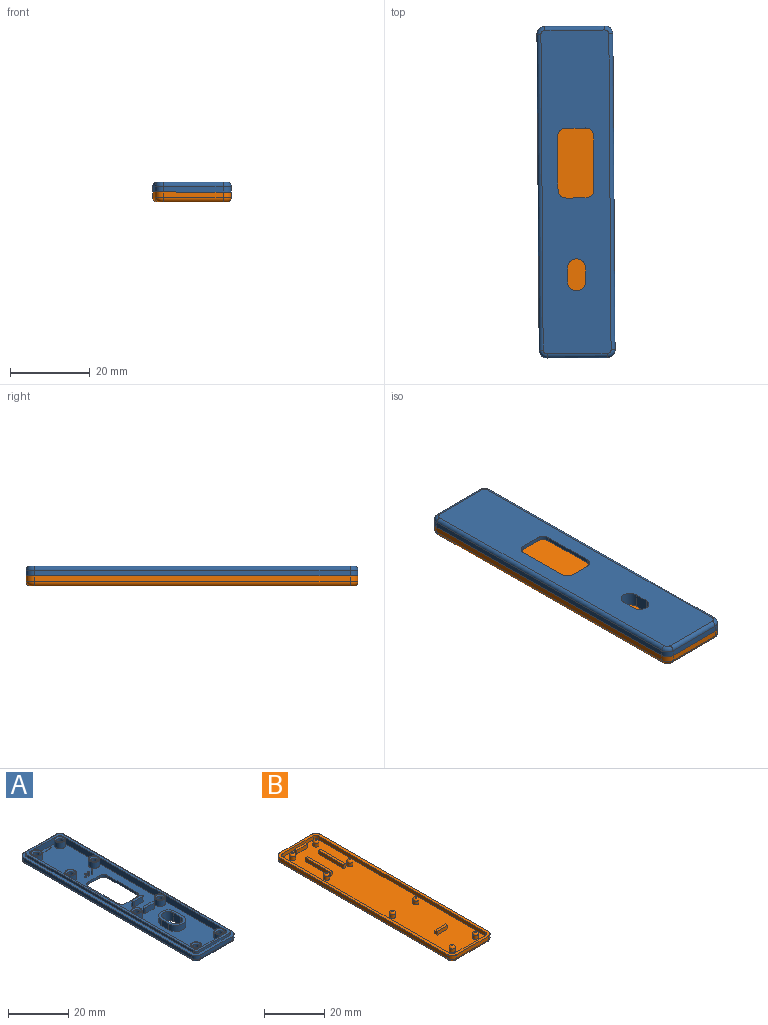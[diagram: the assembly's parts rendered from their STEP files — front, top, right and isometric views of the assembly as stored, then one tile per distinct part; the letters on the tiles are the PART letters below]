
ASSEMBLY  parts=2 mates=1
PART A: 113 faces, bbox 19.3x83.3x3.5 mm
  f0: plane 79x15mm, normal (0,0,1), area 873.3mm2, adj f2,f13,f14,f15,f16,f17,f21,f25
  f1: plane 81x17mm, normal (0,0,-1), area 1190.4mm2, adj f35,f36,f37,f38,f68,f69,f77,f78
  f2: plane 13.4x2.5mm, normal (0,-1,0), area 33mm2, adj f0,f12,f17,f18,f51,f90,f92
  f3: plane 83x19mm, normal (0,0,1), area 217.6mm2, adj f4,f5,f6,f7,f8,f9,f10,f11
  f4: plane 15x1.5mm, normal (0,-1,0), area 22.5mm2, adj f3,f73,f76,f80
  f5: plane 79x1.5mm, normal (1,0,0), area 118.5mm2, adj f3,f73,f74,f84
  f6: plane 15x1.5mm, normal (0,1,0), area 22.5mm2, adj f3,f74,f75,f81
  f7: plane 79x1.5mm, normal (-1,0,0), area 118.5mm2, adj f3,f75,f76,f77
  f8: plane 14.2x1mm, normal (0,-1,0), area 14.2mm2, adj f3,f12,f85,f88
  f9: plane 78.2x1mm, normal (1,0,0), area 78.2mm2, adj f3,f12,f85,f86
  f10: plane 14.2x1mm, normal (0,1,0), area 14.2mm2, adj f3,f12,f86,f87
  f11: plane 78.2x1mm, normal (-1,0,0), area 78.2mm2, adj f3,f12,f87,f88
  f12: plane 80.8x16.8mm, normal (0,0,1), area 171.5mm2, adj f2,f8,f9,f10,f11,f13,f14,f15
  f13: plane 77.4x2.5mm, normal (1,0,0), area 193.5mm2, adj f0,f12,f91,f92
  f14: plane 13.4x2.5mm, normal (0,1,0), area 33.5mm2, adj f0,f12,f89,f91
  f15: plane 77.4x2.5mm, normal (-1,0,0), area 193.5mm2, adj f0,f12,f89,f90
  f16: plane 5x0.1mm, normal (0,-1,0), area 0.5mm2, adj f0,f17,f18,f51
  f17: plane 1x0.1mm, normal (-1,0,0), area 0.1mm2, adj f0,f2,f16,f18
  f18: plane 5x1mm, normal (0,0,1), area 5mm2, adj f2,f16,f17,f51
  f19: plane 3.7x3.7mm, normal (0,0,1), area 2.2mm2, adj f21,f97
  f20: cylinder r=1.15mm len=2.3mm, axis (0,0,-1), area 14.5mm2, adj f22,f97
  f21: cylinder r=1.85mm len=3.7mm, axis (0,0,-1), area 29.1mm2, adj f0,f19
  f22: plane 2.3x2.3mm, normal (0,0,1), area 4.2mm2, adj f20
  f23: plane 3.7x3.7mm, normal (0,0,1), area 2.2mm2, adj f25,f100
  f24: cylinder r=1.15mm len=2.3mm, axis (0,0,-1), area 14.5mm2, adj f26,f100
  f25: cylinder r=1.85mm len=3.7mm, axis (0,0,-1), area 29.1mm2, adj f0,f23
  f26: plane 2.3x2.3mm, normal (0,0,1), area 4.2mm2, adj f24
  f27: plane 3.7x3.7mm, normal (0,0,1), area 2.2mm2, adj f29,f99
  f28: cylinder r=1.15mm len=2.3mm, axis (0,0,-1), area 14.5mm2, adj f30,f99
  f29: cylinder r=1.85mm len=3.7mm, axis (0,0,-1), area 29.1mm2, adj f0,f27
  f30: plane 2.3x2.3mm, normal (0,0,1), area 4.2mm2, adj f28
  f31: plane 3.7x3.7mm, normal (0,0,1), area 2.2mm2, adj f33,f98
  f32: cylinder r=1.15mm len=2.3mm, axis (0,0,-1), area 14.5mm2, adj f34,f98
  f33: cylinder r=1.85mm len=3.7mm, axis (0,0,-1), area 29.1mm2, adj f0,f31
  f34: plane 2.3x2.3mm, normal (0,0,1), area 4.2mm2, adj f32
  f35: plane 5x1mm, normal (0,1,0), area 5mm2, adj f0,f1,f105,f107
  f36: plane 5x1mm, normal (0,-1,0), area 5mm2, adj f0,f1,f106,f108
  f37: plane 13.5x1mm, normal (1,0,0), area 13.5mm2, adj f0,f1,f107,f108
  f38: plane 3.5x3.5mm, normal (1,0,0), area 12.2mm2, adj f1,f39,f101,f102
  f39: plane 10x6.5mm, normal (0,0,1), area 24.3mm2, adj f38,f40,f69,f70,f101,f102,f103,f104
  f40: plane 3.5x2.5mm, normal (-1,0,0), area 8.8mm2, adj f0,f39,f103,f104
  f41: plane 0.5x0.5mm, normal (0,0,1), area 0.2mm2, adj f42
  f42: cylinder r=0.25mm len=1.5mm, axis (0,0,-1), area 2.4mm2, adj f0,f41
  f43: plane 0.5x0.5mm, normal (0,0,1), area 0.2mm2, adj f44
  f44: cylinder r=0.25mm len=1.5mm, axis (0,0,-1), area 2.4mm2, adj f0,f43
  f45: plane 5x1mm, normal (0,0,1), area 4.8mm2, adj f46,f47,f110,f112
  f46: plane 4x2.25mm, normal (0,1,0), area 9mm2, adj f0,f45,f110,f112
  f47: plane 4x2.25mm, normal (0,-1,0), area 9mm2, adj f0,f45,f110,f112
  f48: plane 5x1mm, normal (0,0,1), area 4.8mm2, adj f49,f50,f109,f111
  f49: plane 4x2.3mm, normal (0,1,0), area 9.2mm2, adj f0,f48,f109,f111
  f50: plane 4x2.3mm, normal (0,-1,0), area 9.2mm2, adj f0,f48,f109,f111
  f51: plane 1x0.1mm, normal (1,0,0), area 0.1mm2, adj f0,f2,f16,f18
  f52: plane 3.7x3.7mm, normal (0,0,1), area 2.2mm2, adj f53,f93
  f53: cylinder r=1.85mm len=3.7mm, axis (0,0,-1), area 29.1mm2, adj f0,f52
  f54: cylinder r=1.15mm len=2.3mm, axis (0,0,-1), area 14.5mm2, adj f55,f93
  f55: plane 2.3x2.3mm, normal (0,0,1), area 4.2mm2, adj f54
  f56: plane 3.7x3.7mm, normal (0,0,1), area 2.2mm2, adj f57,f96
  f57: cylinder r=1.85mm len=3.7mm, axis (0,0,-1), area 29.1mm2, adj f0,f56
  f58: cylinder r=1.15mm len=2.3mm, axis (0,0,-1), area 14.5mm2, adj f59,f96
  f59: plane 2.3x2.3mm, normal (0,0,1), area 4.2mm2, adj f58
  f60: plane 3.7x3.7mm, normal (0,0,1), area 2.2mm2, adj f61,f95
  f61: cylinder r=1.85mm len=3.7mm, axis (0,0,-1), area 29.1mm2, adj f0,f60
  f62: cylinder r=1.15mm len=2.3mm, axis (0,0,-1), area 14.5mm2, adj f63,f95
  f63: plane 2.3x2.3mm, normal (0,0,1), area 4.2mm2, adj f62
  f64: plane 3.7x3.7mm, normal (0,0,1), area 2.2mm2, adj f65,f94
  f65: cylinder r=1.85mm len=3.7mm, axis (0,0,-1), area 29.1mm2, adj f0,f64
  f66: cylinder r=1.15mm len=2.3mm, axis (0,0,-1), area 14.5mm2, adj f67,f94
  f67: plane 2.3x2.3mm, normal (0,0,1), area 4.2mm2, adj f66
  f68: plane 13.5x1mm, normal (-1,0,0), area 13.5mm2, adj f0,f1,f105,f106
  f69: plane 3.5x3.5mm, normal (-1,0,0), area 12.2mm2, adj f1,f39,f101,f102
  f70: plane 3.5x2.5mm, normal (1,0,0), area 8.8mm2, adj f0,f39,f103,f104
  f71: plane 0.5x0.5mm, normal (0,0,1), area 0.2mm2, adj f72
  f72: cylinder r=0.25mm len=1.5mm, axis (0,0,-1), area 2.4mm2, adj f0,f71
  f73: cylinder r=2mm len=2mm, axis (0,0,1), area 4.7mm2, adj f3,f4,f5,f82
  f74: cylinder r=2mm len=2mm, axis (0,0,-1), area 4.7mm2, adj f3,f5,f6,f83
  f75: cylinder r=2mm len=2mm, axis (0,0,1), area 4.7mm2, adj f3,f6,f7,f79
  f76: cylinder r=2mm len=2mm, axis (0,0,-1), area 4.7mm2, adj f3,f4,f7,f78
  f77: cylinder r=1mm len=79mm, axis (0,-1,0), area 124.1mm2, adj f1,f7,f78,f79
  f78: torus R=1mm, axis (0,0,1), area 4mm2, adj f1,f76,f77,f80
  f79: torus R=1mm, axis (0,0,1), area 4mm2, adj f1,f75,f77,f81
  f80: cylinder r=1mm len=15mm, axis (1,0,0), area 23.6mm2, adj f1,f4,f78,f82
  f81: cylinder r=1mm len=15mm, axis (-1,0,0), area 23.6mm2, adj f1,f6,f79,f83
  f82: torus R=1mm, axis (0,0,1), area 4mm2, adj f1,f73,f80,f84
  f83: torus R=1mm, axis (0,0,1), area 4mm2, adj f1,f74,f81,f84
  f84: cylinder r=1mm len=79mm, axis (0,1,0), area 124.1mm2, adj f1,f5,f82,f83
  f85: cylinder r=1.3mm len=1.3mm, axis (0,0,1), area 2mm2, adj f3,f8,f9,f12
  f86: cylinder r=1.3mm len=1.3mm, axis (0,0,-1), area 2mm2, adj f3,f9,f10,f12
  f87: cylinder r=1.3mm len=1.3mm, axis (0,0,1), area 2mm2, adj f3,f10,f11,f12
  f88: cylinder r=1.3mm len=1.3mm, axis (0,0,-1), area 2mm2, adj f3,f8,f11,f12
  f89: cylinder r=0.8mm len=2.5mm, axis (0,0,1), area 3.1mm2, adj f0,f12,f14,f15
  f90: cylinder r=0.8mm len=2.5mm, axis (0,0,-1), area 3.1mm2, adj f0,f2,f12,f15
  f91: cylinder r=0.8mm len=2.5mm, axis (0,0,-1), area 3.1mm2, adj f0,f12,f13,f14
  f92: cylinder r=0.8mm len=2.5mm, axis (0,0,1), area 3.1mm2, adj f0,f2,f12,f13
  f93: torus R=1.65mm, axis (0,0,1), area 6.6mm2, adj f52,f54
  f94: torus R=1.65mm, axis (0,0,1), area 6.6mm2, adj f64,f66
  f95: torus R=1.65mm, axis (0,0,1), area 6.6mm2, adj f60,f62
  f96: torus R=1.65mm, axis (0,0,1), area 6.6mm2, adj f56,f58
  f97: torus R=1.65mm, axis (0,0,1), area 6.6mm2, adj f19,f20
  f98: torus R=1.65mm, axis (0,0,1), area 6.6mm2, adj f31,f32
  f99: torus R=1.65mm, axis (0,0,1), area 6.6mm2, adj f27,f28
  f100: torus R=1.65mm, axis (0,0,1), area 6.6mm2, adj f23,f24
  f101: cylinder r=2.25mm len=4.5mm, axis (0,0,1), area 24.7mm2, adj f1,f38,f39,f69
  f102: cylinder r=2.25mm len=4.5mm, axis (0,0,-1), area 24.7mm2, adj f1,f38,f39,f69
  f103: cylinder r=3.25mm len=6.5mm, axis (0,0,-1), area 25.5mm2, adj f0,f39,f40,f70
  f104: cylinder r=3.25mm len=6.5mm, axis (0,0,-1), area 25.5mm2, adj f0,f39,f40,f70
  f105: cylinder r=2mm len=2mm, axis (0,0,1), area 3.1mm2, adj f0,f1,f35,f68
  f106: cylinder r=2mm len=2mm, axis (0,0,-1), area 3.1mm2, adj f0,f1,f36,f68
  f107: cylinder r=2mm len=2mm, axis (0,0,-1), area 3.1mm2, adj f0,f1,f35,f37
  f108: cylinder r=2mm len=2mm, axis (0,0,1), area 3.1mm2, adj f0,f1,f36,f37
  f109: cylinder r=0.5mm len=2.3mm, axis (0,0,1), area 3.6mm2, adj f0,f48,f49,f50
  f110: cylinder r=0.5mm len=2.25mm, axis (0,0,1), area 3.5mm2, adj f0,f45,f46,f47
  f111: cylinder r=0.5mm len=2.3mm, axis (0,0,1), area 3.6mm2, adj f0,f48,f49,f50
  f112: cylinder r=0.5mm len=2.25mm, axis (0,0,1), area 3.5mm2, adj f0,f45,f46,f47
PART B: 71 faces, bbox 19.3x83.3x3.3 mm
  f0: plane 81x17mm, normal (0,0,1), area 1316.2mm2, adj f7,f8,f9,f10,f12,f13,f14,f16
  f1: plane 15x1.5mm, normal (0,-1,0), area 22.5mm2, adj f5,f32,f35,f62
  f2: plane 79x1.5mm, normal (1,0,0), area 118.5mm2, adj f5,f32,f33,f59
  f3: plane 15x1.5mm, normal (0,1,0), area 22.5mm2, adj f5,f33,f34,f63
  f4: plane 79x1.5mm, normal (-1,0,0), area 118.5mm2, adj f5,f34,f35,f66
  f5: plane 83x19mm, normal (0,0,1), area 198mm2, adj f1,f2,f3,f4,f7,f8,f9,f10
  f6: plane 81x17mm, normal (0,0,-1), area 1376.1mm2, adj f59,f60,f61,f62,f63,f64,f65,f66
  f7: plane 78.4x1.5mm, normal (-1,0,0), area 117.6mm2, adj f0,f5,f67,f68
  f8: plane 14.4x1.5mm, normal (0,1,0), area 21.6mm2, adj f0,f5,f67,f69
  f9: plane 14.4x1.5mm, normal (0,-1,0), area 21.6mm2, adj f0,f5,f68,f70
  f10: plane 78.4x1.5mm, normal (1,0,0), area 117.6mm2, adj f0,f5,f69,f70
  f11: plane 5.1x1mm, normal (0,0,1), area 5.1mm2, adj f12,f13,f14,f58
  f12: plane 5.1x1.5mm, normal (0,1,0), area 7.7mm2, adj f0,f11,f14,f58
  f13: plane 5.1x1.5mm, normal (0,-1,0), area 7.7mm2, adj f0,f11,f14,f58
  f14: plane 1.5x1mm, normal (-1,0,0), area 1.5mm2, adj f0,f11,f12,f13
  f15: plane 5.1x1mm, normal (0,0,1), area 5.1mm2, adj f16,f17,f18,f57
  f16: plane 5.1x1.5mm, normal (0,1,0), area 7.7mm2, adj f0,f15,f18,f57
  f17: plane 5.1x1.5mm, normal (0,-1,0), area 7.7mm2, adj f0,f15,f18,f57
  f18: plane 1.5x1mm, normal (-1,0,0), area 1.5mm2, adj f0,f15,f16,f17
  f19: plane 12x1mm, normal (0,0,1), area 12mm2, adj f20,f21,f22,f23
  f20: plane 12x1.5mm, normal (-1,0,0), area 18mm2, adj f0,f19,f21,f22
  f21: plane 1.5x1mm, normal (0,-1,0), area 1.5mm2, adj f0,f19,f20,f23
  f22: plane 1.5x1mm, normal (0,1,0), area 1.5mm2, adj f0,f19,f20,f23
  f23: plane 12x1.5mm, normal (1,0,0), area 18mm2, adj f0,f19,f21,f22
  f24: cylinder r=1mm len=2mm, axis (0,0,-1), area 9.4mm2, adj f0,f36
  f25: plane 0.5x0.5mm, normal (0,0,1), area 0.2mm2, adj f36
  f26: cylinder r=1mm len=2mm, axis (0,0,-1), area 9.4mm2, adj f0,f39
  f27: plane 0.5x0.5mm, normal (0,0,1), area 0.2mm2, adj f39
  f28: cylinder r=1mm len=2mm, axis (0,0,-1), area 9.4mm2, adj f0,f38
  f29: plane 0.5x0.5mm, normal (0,0,1), area 0.2mm2, adj f38
  f30: cylinder r=1mm len=2mm, axis (0,0,-1), area 9.4mm2, adj f0,f37
  f31: plane 0.5x0.5mm, normal (0,0,1), area 0.2mm2, adj f37
  f32: cylinder r=2mm len=2mm, axis (0,0,1), area 4.7mm2, adj f1,f2,f5,f60
  f33: cylinder r=2mm len=2mm, axis (0,0,-1), area 4.7mm2, adj f2,f3,f5,f61
  f34: cylinder r=2mm len=2mm, axis (0,0,1), area 4.7mm2, adj f3,f4,f5,f65
  f35: cylinder r=2mm len=2mm, axis (0,0,-1), area 4.7mm2, adj f1,f4,f5,f64
  f36: torus R=0.25mm, axis (0,0,1), area 5.4mm2, adj f24,f25
  f37: torus R=0.25mm, axis (0,0,1), area 5.4mm2, adj f30,f31
  f38: torus R=0.25mm, axis (0,0,1), area 5.4mm2, adj f28,f29
  f39: torus R=0.25mm, axis (0,0,1), area 5.4mm2, adj f26,f27
  f40: plane 0.5x0.5mm, normal (0,0,1), area 0.2mm2, adj f41
  f41: torus R=0.25mm, axis (0,0,1), area 5.4mm2, adj f40,f42
  f42: cylinder r=1mm len=2mm, axis (0,0,-1), area 9.4mm2, adj f0,f41
  f43: plane 0.5x0.5mm, normal (0,0,1), area 0.2mm2, adj f44
  f44: torus R=0.25mm, axis (0,0,1), area 5.4mm2, adj f43,f45
  f45: cylinder r=1mm len=2mm, axis (0,0,-1), area 9.4mm2, adj f0,f44
  f46: plane 0.5x0.5mm, normal (0,0,1), area 0.2mm2, adj f47
  f47: torus R=0.25mm, axis (0,0,1), area 5.4mm2, adj f46,f48
  f48: cylinder r=1mm len=2mm, axis (0,0,-1), area 9.4mm2, adj f0,f47
  f49: plane 0.5x0.5mm, normal (0,0,1), area 0.2mm2, adj f50
  f50: torus R=0.25mm, axis (0,0,1), area 5.4mm2, adj f49,f51
  f51: cylinder r=1mm len=2mm, axis (0,0,-1), area 9.4mm2, adj f0,f50
  f52: plane 12x1mm, normal (0,0,1), area 12mm2, adj f53,f54,f55,f56
  f53: plane 12x1.5mm, normal (-1,0,0), area 18mm2, adj f0,f52,f54,f55
  f54: plane 1.5x1mm, normal (0,1,0), area 1.5mm2, adj f0,f52,f53,f56
  f55: plane 1.5x1mm, normal (0,-1,0), area 1.5mm2, adj f0,f52,f53,f56
  f56: plane 12x1.5mm, normal (1,0,0), area 18mm2, adj f0,f52,f54,f55
  f57: plane 1.5x1mm, normal (1,0,0), area 1.5mm2, adj f0,f15,f16,f17
  f58: plane 1.5x1mm, normal (1,0,0), area 1.5mm2, adj f0,f11,f12,f13
  f59: cylinder r=1mm len=79mm, axis (0,1,0), area 124.1mm2, adj f2,f6,f60,f61
  f60: torus R=1mm, axis (0,0,1), area 4mm2, adj f6,f32,f59,f62
  f61: torus R=1mm, axis (0,0,1), area 4mm2, adj f6,f33,f59,f63
  f62: cylinder r=1mm len=15mm, axis (1,0,0), area 23.6mm2, adj f1,f6,f60,f64
  f63: cylinder r=1mm len=15mm, axis (-1,0,0), area 23.6mm2, adj f3,f6,f61,f65
  f64: torus R=1mm, axis (0,0,1), area 4mm2, adj f6,f35,f62,f66
  f65: torus R=1mm, axis (0,0,1), area 4mm2, adj f6,f34,f63,f66
  f66: cylinder r=1mm len=79mm, axis (0,-1,0), area 124.1mm2, adj f4,f6,f64,f65
  f67: cylinder r=1.3mm len=1.5mm, axis (0,0,1), area 3.1mm2, adj f0,f5,f7,f8
  f68: cylinder r=1.3mm len=1.5mm, axis (0,0,-1), area 3.1mm2, adj f0,f5,f7,f9
  f69: cylinder r=1.3mm len=1.5mm, axis (0,0,-1), area 3.1mm2, adj f0,f5,f8,f10
  f70: cylinder r=1.3mm len=1.5mm, axis (0,0,1), area 3.1mm2, adj f0,f5,f9,f10
PLACE A rot(axis=(0,-1,0),180deg) t=(-1.33,4.08,-11.38)mm
PLACE B rot(axis=(0,0,1),0.4deg) t=(-1.33,4.08,-16.38)mm
MATE fastened A.f3 <-> B.f5  axis (0,0,-1) through (8.45,-35.36,-13.88)mm
